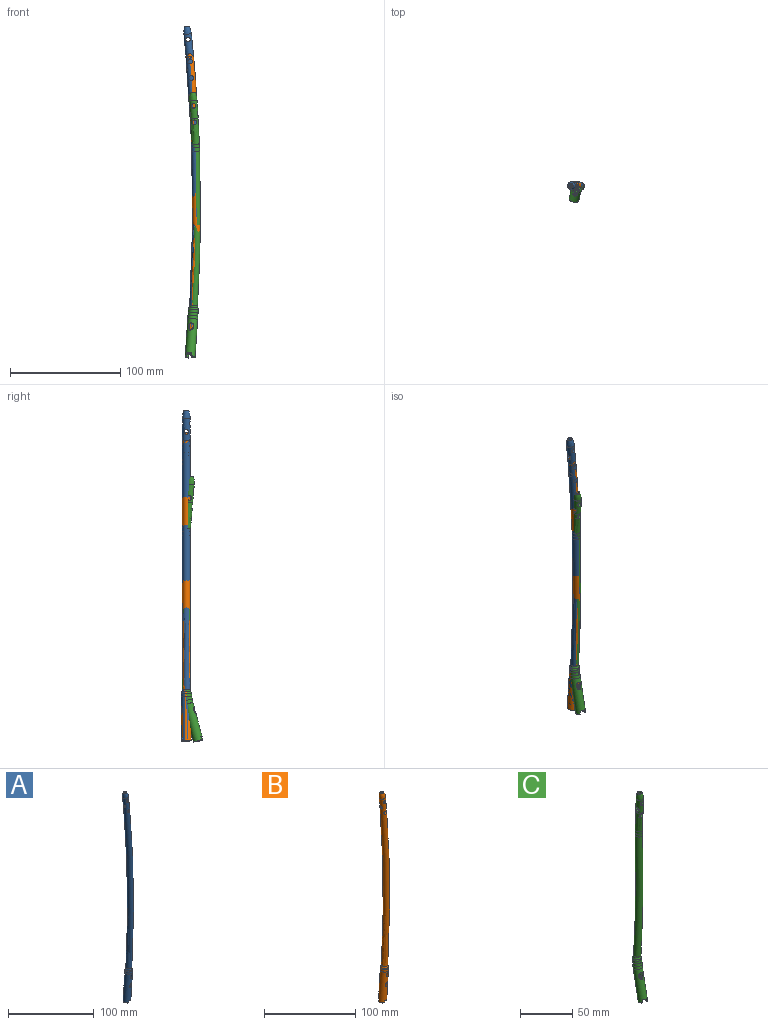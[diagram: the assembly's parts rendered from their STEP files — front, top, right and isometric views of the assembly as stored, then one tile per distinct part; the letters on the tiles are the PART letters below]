
ASSEMBLY  parts=3 mates=2
PART A: 51 faces, bbox 21x14.1x300.8 mm
  f0: cylinder r=4.5mm len=40.6mm, axis (-0.07,0,-1), area 1023.9mm2, adj f7,f8,f9,f15,f16,f20,f23,f25
  f1: cylinder r=2.56mm len=32.3mm, axis (0.07,0,1), area 376.8mm2, adj f2,f7,f8,f24,f43,f44,f46,f47
  f2: cylinder r=2.56mm len=5.2mm, axis (0.07,0,1), area 3.5mm2, adj f1,f3,f49,f50
  f3: cylinder r=2.56mm len=5.2mm, axis (0.07,0,1), area 3.5mm2, adj f2,f4,f49,f50
  f4: cylinder r=2.56mm len=5.2mm, axis (0.07,0,1), area 3.5mm2, adj f3,f5,f49,f50
  f5: cylinder r=2.56mm len=5.19mm, axis (0.07,0,1), area 3.4mm2, adj f4,f6,f23,f49,f50
  f6: cylinder r=2.56mm len=1.34mm, axis (0.07,0,1), area 0.1mm2, adj f5,f23,f50
  f7: cylinder r=2.38mm len=5.51mm, axis (0.19,-0.84,-0.51), area 23.4mm2, adj f0,f1,f45,f46
  f8: cylinder r=2.38mm len=5.45mm, axis (0.19,-0.84,-0.51), area 22mm2, adj f0,f1,f42,f43
  f9: cylinder r=2.38mm len=2.3mm, axis (0.19,-0.84,-0.51), area 0mm2, adj f0,f43
  f10: torus R=1450mm, axis (0,-1,0), area 40.5mm2, adj f30,f31
  f11: torus R=1450mm, axis (0,-1,0), area 5330.2mm2, adj f22,f29,f30,f31,f40
  f12: torus R=1450mm, axis (0,-1,0), area 2324.4mm2, adj f24,f30
  f13: torus R=1450mm, axis (0,-1,0), area 39.9mm2, adj f29,f31
  f14: torus R=1450mm, axis (0,-1,0), area 107mm2, adj f19,f29
  f15: plane 6.97x2.83mm, normal (-0.07,0,-1), area 7.6mm2, adj f0,f17,f33,f34
  f16: plane 6.97x2.83mm, normal (-0.07,0,-1), area 7.6mm2, adj f0,f18,f32,f35
  f17: cylinder r=3.28mm len=4.95mm, axis (0.07,0,1), area 14.5mm2, adj f15,f23,f26,f27,f33,f34,f38,f39
  f18: cylinder r=3.28mm len=4.95mm, axis (0.07,0,1), area 14.5mm2, adj f16,f23,f25,f28,f32,f35,f36,f37
  f19: plane 3.61x3.59mm, normal (-0.11,0,0.99), area 2.2mm2, adj f14,f41
  f20: torus R=1450mm, axis (0,-1,0), area 78.7mm2, adj f0,f21
  f21: bspline ~9.01x8.99mm, area 41.9mm2, adj f20,f22
  f22: bspline ~8.27x8.25mm, area 58.9mm2, adj f11,f21
  f23: plane 9.27x6.81mm, normal (-0.07,0,-1), area 17.8mm2, adj f0,f5,f6,f17,f18,f36,f37,f38
  f24: cone r=2.56mm half-angle=59deg, axis (-0.07,0,-1), area 14.5mm2, adj f1,f12
  f25: plane 2.37x1.54mm, normal (0.96,0.26,-0.06), area 3.8mm2, adj f0,f18,f35,f36
  f26: plane 2.37x1.54mm, normal (-0.96,-0.26,0.06), area 3.8mm2, adj f0,f17,f34,f39
  f27: plane 2.37x1.54mm, normal (-0.96,-0.26,0.06), area 3.8mm2, adj f0,f17,f33,f38
  f28: plane 2.37x1.54mm, normal (0.96,0.26,-0.06), area 3.8mm2, adj f0,f18,f32,f37
  f29: cylinder r=2.1mm len=7mm, axis (0,1,0), area 65.7mm2, adj f11,f13,f14
  f30: cylinder r=2.1mm len=7mm, axis (0,1,0), area 65.8mm2, adj f10,f11,f12
  f31: cylinder r=2.1mm len=7.38mm, axis (-1,0,-0.1), area 65.7mm2, adj f10,f11,f13
  f32: plane 1.79x0.76mm, normal (0.63,0.18,-0.75), area 0.6mm2, adj f0,f16,f18,f28
  f33: plane 1.92x0.6mm, normal (-0.73,-0.18,-0.66), area 0.6mm2, adj f0,f15,f17,f27
  f34: plane 1.79x0.73mm, normal (-0.73,-0.18,-0.66), area 0.6mm2, adj f0,f15,f17,f26
  f35: plane 1.92x0.63mm, normal (0.63,0.18,-0.75), area 0.6mm2, adj f0,f16,f18,f25
  f36: cylinder r=0.4mm len=1.87mm, axis (0.26,-0.97,-0.02), area 1mm2, adj f0,f18,f23,f25
  f37: cylinder r=0.4mm len=1.87mm, axis (0.26,-0.97,-0.02), area 1mm2, adj f0,f18,f23,f28
  f38: cylinder r=0.4mm len=1.87mm, axis (-0.26,0.97,0.02), area 1mm2, adj f0,f17,f23,f27
  f39: cylinder r=0.4mm len=1.87mm, axis (-0.26,0.97,0.02), area 1mm2, adj f0,f17,f23,f26
  f40: revolved ~7.49x7.08mm, area 136.7mm2, adj f11,f41
  f41: bspline ~4.55x4.52mm, area 7.9mm2, adj f19,f40
  f42: cylinder r=2.38mm len=4.97mm, axis (-0.23,0.68,-0.69), area 9.6mm2, adj f0,f8
  f43: cylinder r=2.38mm len=6.33mm, axis (-0.23,0.68,-0.69), area 32.6mm2, adj f0,f1,f8,f9
  f44: cylinder r=2.38mm len=8.85mm, axis (-0.23,0.68,-0.69), area 49.3mm2, adj f0,f1
  f45: cylinder r=2.38mm len=4.1mm, axis (-0.23,0.68,-0.69), area 0mm2, adj f0,f7
  f46: cylinder r=2.38mm len=6.42mm, axis (-0.23,0.68,-0.69), area 32mm2, adj f0,f1,f7
  f47: plane 1.05x0.47mm, normal (0.76,0.65,-0.05), area 0.4mm2, adj f1,f48,f49,f50
  f48: cylinder r=3.17mm len=7.07mm, axis (0.07,0,1), area 33.4mm2, adj f23,f47,f49,f50
  f49: bspline ~7.58x6.67mm, area 69.5mm2, adj f1,f2,f3,f4,f5,f23,f47,f48
  f50: bspline ~6.68x6.58mm, area 62.6mm2, adj f1,f2,f3,f4,f5,f6,f23,f47
PART B: 51 faces, bbox 18.6x14.1x280.8 mm
  f0: cylinder r=4.5mm len=40.6mm, axis (-0.07,0,-1), area 1023.7mm2, adj f7,f8,f9,f15,f16,f20,f23,f25
  f1: cylinder r=2.56mm len=32.3mm, axis (0.07,0,1), area 376.8mm2, adj f5,f7,f8,f24,f43,f44,f46,f47
  f2: cylinder r=2.56mm len=5.19mm, axis (0.07,0,1), area 3.4mm2, adj f3,f6,f23,f49,f50
  f3: cylinder r=2.56mm len=5.2mm, axis (0.07,0,1), area 3.5mm2, adj f2,f4,f49,f50
  f4: cylinder r=2.56mm len=5.2mm, axis (0.07,0,1), area 3.5mm2, adj f3,f5,f49,f50
  f5: cylinder r=2.56mm len=5.2mm, axis (0.07,0,1), area 3.5mm2, adj f1,f4,f49,f50
  f6: cylinder r=2.56mm len=1.34mm, axis (0.07,0,1), area 0.1mm2, adj f2,f23,f49
  f7: cylinder r=2.38mm len=5.51mm, axis (0.19,-0.84,-0.51), area 23.4mm2, adj f0,f1,f45,f46
  f8: cylinder r=2.38mm len=5.45mm, axis (0.19,-0.84,-0.51), area 22mm2, adj f0,f1,f42,f43
  f9: cylinder r=2.38mm len=2.3mm, axis (0.19,-0.84,-0.51), area 0mm2, adj f0,f43
  f10: torus R=1450mm, axis (0,-1,0), area 40.5mm2, adj f30,f31
  f11: torus R=1450mm, axis (0,-1,0), area 4885.8mm2, adj f22,f29,f30,f31,f40
  f12: torus R=1450mm, axis (0,-1,0), area 2121.5mm2, adj f24,f30
  f13: torus R=1450mm, axis (0,-1,0), area 40mm2, adj f29,f31
  f14: torus R=1450mm, axis (0,-1,0), area 106.9mm2, adj f19,f29
  f15: plane 6.97x2.83mm, normal (-0.07,0,-1), area 7.6mm2, adj f0,f17,f33,f34
  f16: plane 6.97x2.83mm, normal (-0.07,0,-1), area 7.6mm2, adj f0,f18,f32,f35
  f17: cylinder r=3.28mm len=4.95mm, axis (0.07,0,1), area 14.5mm2, adj f15,f23,f26,f27,f33,f34,f38,f39
  f18: cylinder r=3.28mm len=4.95mm, axis (0.07,0,1), area 14.5mm2, adj f16,f23,f25,f28,f32,f35,f36,f37
  f19: plane 3.61x3.59mm, normal (-0.1,0,1), area 2.1mm2, adj f14,f41
  f20: torus R=1450mm, axis (0,-1,0), area 84.5mm2, adj f0,f21
  f21: bspline ~9.01x8.99mm, area 41.8mm2, adj f20,f22
  f22: bspline ~8.27x8.25mm, area 58.9mm2, adj f11,f21
  f23: plane 9.27x6.81mm, normal (-0.07,0,-1), area 17.8mm2, adj f0,f2,f6,f17,f18,f36,f37,f38
  f24: cone r=2.56mm half-angle=59deg, axis (-0.07,0,-1), area 14.5mm2, adj f1,f12
  f25: plane 2.37x1.54mm, normal (0.96,0.26,-0.06), area 3.8mm2, adj f0,f18,f35,f36
  f26: plane 2.37x1.54mm, normal (-0.96,-0.26,0.06), area 3.8mm2, adj f0,f17,f34,f39
  f27: plane 2.37x1.54mm, normal (-0.96,-0.26,0.06), area 3.8mm2, adj f0,f17,f33,f38
  f28: plane 2.37x1.54mm, normal (0.96,0.26,-0.06), area 3.8mm2, adj f0,f18,f32,f37
  f29: cylinder r=2.1mm len=7mm, axis (0,1,0), area 65.7mm2, adj f11,f13,f14
  f30: cylinder r=2.1mm len=7mm, axis (0,1,0), area 65.8mm2, adj f10,f11,f12
  f31: cylinder r=2.1mm len=7.33mm, axis (-1,0,-0.09), area 67.1mm2, adj f10,f11,f13
  f32: plane 1.79x0.76mm, normal (0.63,0.18,-0.75), area 0.6mm2, adj f0,f16,f18,f28
  f33: plane 1.92x0.6mm, normal (-0.73,-0.18,-0.66), area 0.6mm2, adj f0,f15,f17,f27
  f34: plane 1.79x0.73mm, normal (-0.73,-0.18,-0.66), area 0.6mm2, adj f0,f15,f17,f26
  f35: plane 1.92x0.63mm, normal (0.63,0.18,-0.75), area 0.6mm2, adj f0,f16,f18,f25
  f36: cylinder r=0.4mm len=1.87mm, axis (0.26,-0.97,-0.02), area 1mm2, adj f0,f18,f23,f25
  f37: cylinder r=0.4mm len=1.87mm, axis (0.26,-0.97,-0.02), area 1mm2, adj f0,f18,f23,f28
  f38: cylinder r=0.4mm len=1.87mm, axis (-0.26,0.97,0.02), area 1mm2, adj f0,f17,f23,f27
  f39: cylinder r=0.4mm len=1.87mm, axis (-0.26,0.97,0.02), area 1mm2, adj f0,f17,f23,f26
  f40: revolved ~7.42x7.06mm, area 136.8mm2, adj f11,f41
  f41: bspline ~4.55x4.52mm, area 7.9mm2, adj f19,f40
  f42: cylinder r=2.38mm len=4.97mm, axis (-0.23,0.68,-0.69), area 9.6mm2, adj f0,f8
  f43: cylinder r=2.38mm len=6.33mm, axis (-0.23,0.68,-0.69), area 32.6mm2, adj f0,f1,f8,f9
  f44: cylinder r=2.38mm len=8.85mm, axis (-0.23,0.68,-0.69), area 49.3mm2, adj f0,f1
  f45: cylinder r=2.38mm len=4.1mm, axis (-0.23,0.68,-0.69), area 0mm2, adj f0,f7
  f46: cylinder r=2.38mm len=6.42mm, axis (-0.23,0.68,-0.69), area 32mm2, adj f0,f1,f7
  f47: plane 1.05x0.47mm, normal (0.76,0.65,-0.05), area 0.4mm2, adj f1,f48,f49,f50
  f48: cylinder r=3.17mm len=7.07mm, axis (0.07,0,1), area 33.4mm2, adj f23,f47,f49,f50
  f49: bspline ~6.68x6.58mm, area 62.6mm2, adj f1,f2,f3,f4,f5,f6,f23,f47
  f50: bspline ~7.58x6.67mm, area 69.5mm2, adj f1,f2,f3,f4,f5,f23,f47,f48
PART C: 55 faces, bbox 15.6x20.9x241.4 mm
  f0: cylinder r=4.5mm len=36.04mm, axis (-0.06,-0.26,-0.96), area 895.8mm2, adj f2,f3,f5,f6,f14,f15,f31,f33
  f1: cylinder r=2.56mm len=37.03mm, axis (0.06,0.26,0.96), area 477mm2, adj f2,f5,f31,f32,f51,f52,f54
  f2: cylinder r=2.38mm len=5.68mm, axis (0.18,0.68,-0.71), area 23.4mm2, adj f0,f1,f53,f54
  f3: torus R=50.21mm, axis (1,0,-0.07), area 76.1mm2, adj f0,f4,f52
  f4: torus R=50.22mm, axis (1,0,-0.07), area 89.9mm2, adj f3,f28,f52
  f5: cylinder r=2.38mm len=5.61mm, axis (0.18,0.68,-0.71), area 22mm2, adj f0,f1,f50,f51
  f6: cylinder r=2.38mm len=2.31mm, axis (0.18,0.68,-0.71), area 0mm2, adj f0,f51
  f7: torus R=1461.03mm, axis (0,1,0.09), area 22.8mm2, adj f13,f39
  f8: torus R=1461.03mm, axis (0,1,0.09), area 299.1mm2, adj f11,f38,f39,f48
  f9: torus R=1461.03mm, axis (0,1,0.09), area 39.9mm2, adj f38,f39
  f10: torus R=1461.03mm, axis (0,1,0.09), area 103.2mm2, adj f27,f38
  f11: torus R=1461.07mm, axis (0,1,0.09), area 487.5mm2, adj f8,f18,f37
  f12: torus R=1461.07mm, axis (0,1,0.09), area 183.4mm2, adj f19,f37
  f13: torus R=1461.07mm, axis (0,1,0.09), area 17.7mm2, adj f7,f37
  f14: plane 6.73x2.76mm, normal (-0.06,-0.26,-0.96), area 7.6mm2, adj f0,f16,f41,f42
  f15: plane 6.73x2.76mm, normal (-0.06,-0.26,-0.96), area 7.6mm2, adj f0,f17,f40,f43
  f16: cylinder r=3.28mm len=5.56mm, axis (0.06,0.26,0.96), area 14.5mm2, adj f14,f31,f34,f35,f41,f42,f46,f47
  f17: cylinder r=3.28mm len=5.56mm, axis (0.06,0.26,0.96), area 14.5mm2, adj f15,f31,f33,f36,f40,f43,f44,f45
  f18: torus R=75.02mm, axis (-1,0.05,-0.03), area 72mm2, adj f11,f20
  f19: torus R=75.02mm, axis (-1,0.05,-0.03), area 32.9mm2, adj f12,f21
  f20: torus R=74.99mm, axis (-1,0.05,-0.03), area 72mm2, adj f18,f22
  f21: torus R=74.99mm, axis (-1,0.05,-0.03), area 32.9mm2, adj f19,f23
  f22: torus R=1450mm, axis (0,1,0), area 3081.7mm2, adj f20,f30
  f23: torus R=1450mm, axis (0,1,0), area 1409.6mm2, adj f21,f24
  f24: torus R=50.17mm, axis (-1,0.03,0.06), area 33.3mm2, adj f23,f25
  f25: torus R=50.2mm, axis (-1,0.03,0.06), area 33.3mm2, adj f24,f26
  f26: torus R=50.22mm, axis (-1,0,0.07), area 8.3mm2, adj f25,f32
  f27: plane 3.59x3.58mm, normal (-0.07,-0.09,0.99), area 2.1mm2, adj f10,f49
  f28: torus R=50.2mm, axis (1,-0.03,-0.06), area 85mm2, adj f4,f29
  f29: bspline ~9.01x9.01mm, area 41.9mm2, adj f28,f30
  f30: bspline ~8.27x8.27mm, area 59mm2, adj f22,f29
  f31: plane 8.69x6.54mm, normal (-0.06,-0.26,-0.96), area 23.7mm2, adj f0,f1,f16,f17,f44,f45,f46,f47
  f32: cone r=2.56mm half-angle=59deg, axis (-0.06,-0.26,-0.96), area 14.6mm2, adj f1,f26
  f33: plane 2.69x2.1mm, normal (0.97,-0.25,0), area 3.8mm2, adj f0,f17,f40,f45
  f34: plane 2.69x2.1mm, normal (-0.97,0.25,0), area 3.8mm2, adj f0,f16,f41,f46
  f35: plane 2.69x2.1mm, normal (-0.97,0.25,0), area 3.8mm2, adj f0,f16,f42,f47
  f36: plane 2.69x2.1mm, normal (0.97,-0.25,0), area 3.8mm2, adj f0,f17,f43,f44
  f37: cylinder r=2.1mm len=7.34mm, axis (0,-1,-0.09), area 65.8mm2, adj f11,f12,f13
  f38: cylinder r=2.1mm len=7.34mm, axis (0,-1,-0.09), area 65.8mm2, adj f8,f9,f10
  f39: cylinder r=2.1mm len=7.23mm, axis (-1,0.01,-0.06), area 65.8mm2, adj f7,f8,f9
  f40: plane 1.8x0.73mm, normal (0.64,-0.36,-0.68), area 0.6mm2, adj f0,f15,f17,f33
  f41: plane 1.92x0.63mm, normal (-0.73,-0.01,-0.68), area 0.6mm2, adj f0,f14,f16,f34
  f42: plane 1.67x0.76mm, normal (-0.73,-0.01,-0.68), area 0.6mm2, adj f0,f14,f16,f35
  f43: plane 1.79x0.76mm, normal (0.64,-0.36,-0.68), area 0.6mm2, adj f0,f15,f17,f36
  f44: cylinder r=0.4mm len=1.75mm, axis (0.24,0.93,-0.27), area 1mm2, adj f0,f17,f31,f36
  f45: cylinder r=0.4mm len=1.75mm, axis (0.24,0.93,-0.27), area 1mm2, adj f0,f17,f31,f33
  f46: cylinder r=0.4mm len=1.91mm, axis (-0.24,-0.93,0.27), area 1mm2, adj f0,f16,f31,f34
  f47: cylinder r=0.4mm len=1.91mm, axis (-0.24,-0.93,0.27), area 1mm2, adj f0,f16,f31,f35
  f48: revolved ~7.51x6.99mm, area 274.2mm2, adj f8,f49
  f49: bspline ~4.53x4.52mm, area 7.9mm2, adj f27,f48
  f50: cylinder r=2.38mm len=4.95mm, axis (-0.22,-0.84,-0.49), area 4.6mm2, adj f0,f5
  f51: cylinder r=2.38mm len=6.3mm, axis (-0.22,-0.84,-0.49), area 32.2mm2, adj f0,f1,f5,f6
  f52: cylinder r=2.38mm len=8.82mm, axis (-0.22,-0.84,-0.49), area 47.7mm2, adj f0,f1,f3,f4
  f53: cylinder r=2.38mm len=4.12mm, axis (-0.22,-0.84,-0.49), area 0mm2, adj f0,f2
  f54: cylinder r=2.38mm len=6.39mm, axis (-0.22,-0.84,-0.49), area 32mm2, adj f0,f1,f2
PLACE A t=(-86.24,38.6,-18.83)mm
PLACE B t=(-86.24,38.6,-18.83)mm
PLACE C t=(-86.24,162.48,-18.83)mm
MATE cylindrical C.f22 <-> A.f10  axis (0,1,0) through (-1530.3,38.6,118.28)mm
MATE cylindrical B.f10 <-> C.f22  axis (0,-1,0) through (-1530.3,38.6,118.28)mm
